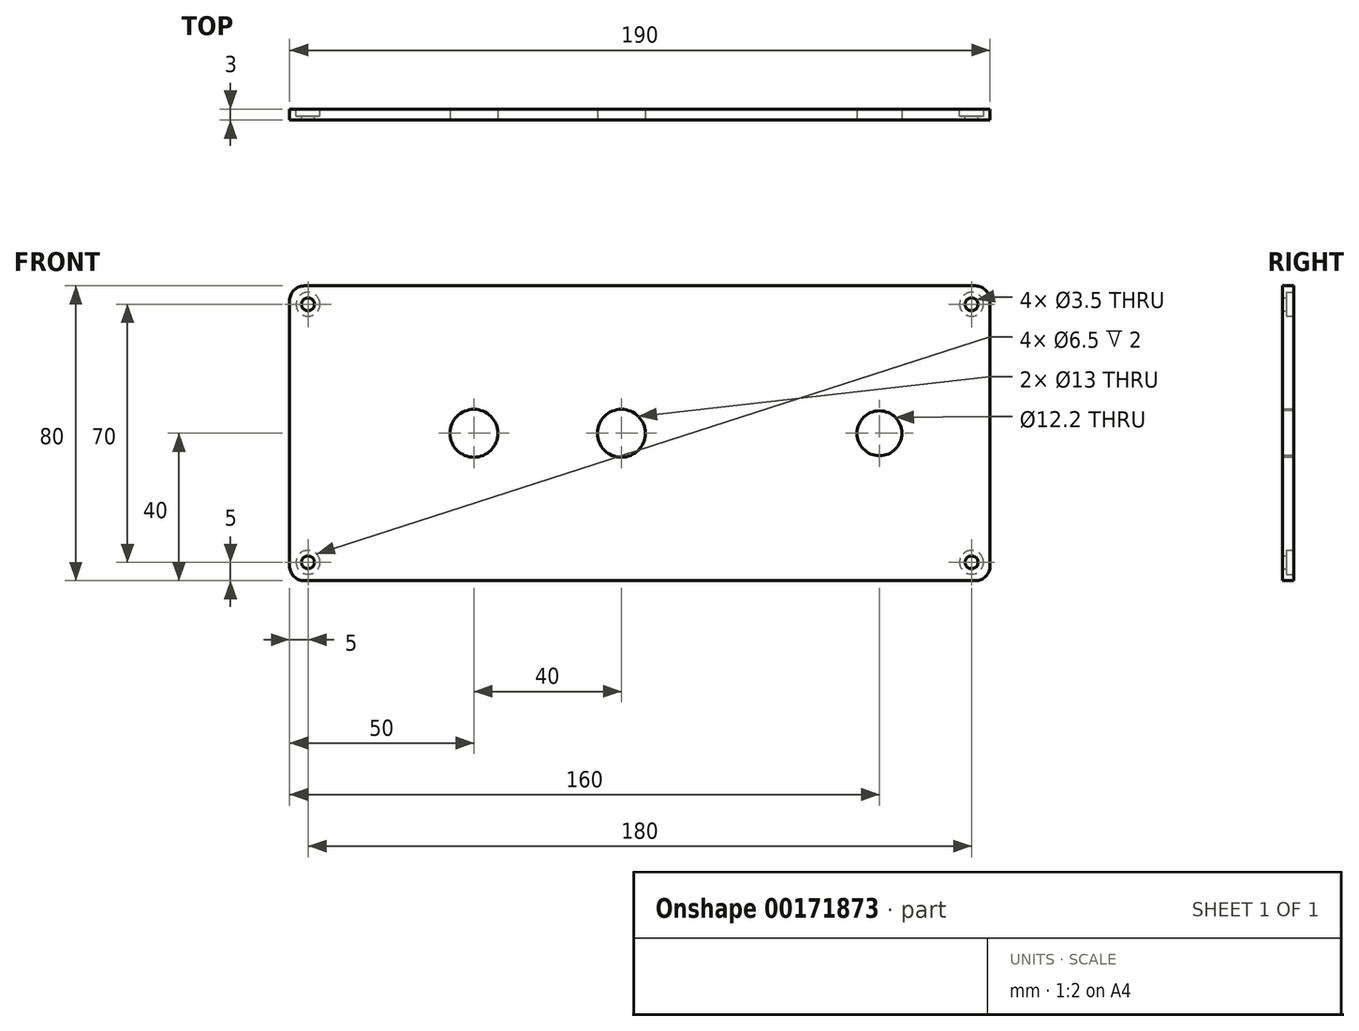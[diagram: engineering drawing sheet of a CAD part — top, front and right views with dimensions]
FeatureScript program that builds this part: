
annotation { "Feature Type Name" : "Feature", "Feature Type Description" : "" }
export const myFeature = defineFeature(function(context is Context, id is Id, definition is map)
    precondition{}
    {
        {
            var Q0;
            Q0=qCreatedBy(makeId("Front.planeOp"),FACE);
            var sketch = newSketch(context, id + "F0", { "sketchPlane" : qUnion([Q0])});
            skLineSegment(sketch, "E0.bottom", {"start": v(91, -40) * mm, "end": v(-91, -40) * mm});
            skLineSegment(sketch, "E0.top", {"start": v(91, 40) * mm, "end": v(-91, 40) * mm});
            skLineSegment(sketch, "E0.left", {"start": v(95, -36) * mm, "end": v(95, 36) * mm});
            skLineSegment(sketch, "E0.right", {"start": v(-95, -36) * mm, "end": v(-95, 36) * mm});
            skPoint(sketch, "E0.middle", {"position": v(0, 0) * mm});
            skLineSegment(sketch, "E1", {"start": v(-95.37, 0) * mm, "end": v(94.03, 0) * mm, "construction": true});
            skLineSegment(sketch, "E2", {"start": v(65, 41.22) * mm, "end": v(65, -44.39) * mm, "construction": true});
            skCircle(sketch, "E3", {"center": v(65, 0) * mm, "radius": 6.1 * mm});
            skPoint(sketch, "E4.visualSharp", {"position": v(-95, 40) * mm});
            skArc(sketch, "E4.filletArc", {"start": v(-91, 40) * mm, "mid": v(-93.83, 38.83) * mm, "end": v(-95, 36) * mm});
            skPoint(sketch, "E5.visualSharp", {"position": v(95, 40) * mm});
            skArc(sketch, "E5.filletArc", {"start": v(95, 36) * mm, "mid": v(93.83, 38.83) * mm, "end": v(91, 40) * mm});
            skPoint(sketch, "E6.visualSharp", {"position": v(95, -40) * mm});
            skArc(sketch, "E6.filletArc", {"start": v(91, -40) * mm, "mid": v(93.83, -38.83) * mm, "end": v(95, -36) * mm});
            skPoint(sketch, "E7.visualSharp", {"position": v(-95, -40) * mm});
            skArc(sketch, "E7.filletArc", {"start": v(-95, -36) * mm, "mid": v(-93.83, -38.83) * mm, "end": v(-91, -40) * mm});
            skPoint(sketch, "E8", {"position": v(65, -1.59) * mm});
            skLineSegment(sketch, "E9", {"start": v(0, 44.53) * mm, "end": v(0, -50.22) * mm, "construction": true});
            skLineSegment(sketch, "E10", {"start": v(-45, 47.95) * mm, "end": v(-45, -55.26) * mm, "construction": true});
            skCircle(sketch, "E11", {"center": v(-5, 0) * mm, "radius": 6.5 * mm});
            skCircle(sketch, "E12", {"center": v(-45, 0) * mm, "radius": 6.5 * mm});
            skLineSegment(sketch, "E13", {"start": v(-5, 53.53) * mm, "end": v(-5, -65.12) * mm, "construction": true});
            skSolve(sketch);
        }
        {
            var Q0;
            Q0=qSketchRegion(id+"F0",true);
            extrude(context, id + "F1", {"entities" : qUnion([Q0]), "oppositeDirection" : true, "depth" : 3 * mm});
        }
        {
            var Q0;
            Q0=makeQuery(id+"F1.opExtrude","CAP_FACE",FACE,{"disambiguationData":[OSD([sQuery(id+"F0.wireOp",EDGE,"E0.bottom"),sQuery(id+"F0.wireOp",EDGE,"E0.top"),sQuery(id+"F0.wireOp",EDGE,"E0.left"),sQuery(id+"F0.wireOp",EDGE,"E0.right"),sQuery(id+"F0.wireOp",EDGE,"4lk48Lhy-GrFW-aCKf-OnOU-HbCll7bjQ1xu"),sQuery(id+"F0.wireOp",EDGE,"0mMwZurY-QGWt-Txsz-sF5m-111nLayFImXw"),sQuery(id+"F0.wireOp",EDGE,"fLtfTxvr-Zha3-877r-iBnS-kihnbPZobVDH"),sQuery(id+"F0.wireOp",EDGE,"zJffz114-50WO-5Ndt-GAZO-3FlYt3vwu0AC"),sQuery(id+"F0.wireOp",EDGE,"zD25MLE3-AGDF-3XqF-6F3W-tQLZOGFrRJCD"),sQuery(id+"F0.wireOp",EDGE,"E3"),sQuery(id+"F0.wireOp",EDGE,"XLCIMhyg-kooL-GM2p-plMR-rza7P0k197HC"),sQuery(id+"F0.wireOp",EDGE,"3nWbJp3Q-z0hA-yKS7-ZoX7-3HNBMeytwRPm"),sQuery(id+"F0.wireOp",EDGE,"r6DEEYF7-k2yr-EeVm-i986-j8R7pWTw2rao"),sQuery(id+"F0.wireOp",EDGE,"dViKmaIw-3wPx-OBVm-rrEE-0ZRbR81GTxym"),sQuery(id+"F0.wireOp",EDGE,"E4.filletArc"),sQuery(id+"F0.wireOp",EDGE,"E5.filletArc"),sQuery(id+"F0.wireOp",EDGE,"E6.filletArc"),sQuery(id+"F0.wireOp",EDGE,"E7.filletArc")])],"isStart":false});
            var sketch = newSketch(context, id + "F2", { "sketchPlane" : qUnion([Q0])});
            skLineSegment(sketch, "E14", {"start": v(-103.47, 35) * mm, "end": v(120, 35) * mm, "construction": true});
            skLineSegment(sketch, "E15", {"start": v(-90, 42.73) * mm, "end": v(-90, -48.6) * mm, "construction": true});
            skLineSegment(sketch, "E16.MirrorCS", {"start": v(90, 42.73) * mm, "end": v(90, -48.6) * mm, "construction": true});
            skLineSegment(sketch, "E17.MirrorCS", {"start": v(-103.47, -35) * mm, "end": v(120, -35) * mm, "construction": true});
            skPoint(sketch, "E18", {"position": v(-90, 35) * mm});
            skPoint(sketch, "E19", {"position": v(90, 35) * mm});
            skPoint(sketch, "E20", {"position": v(90, -35) * mm});
            skPoint(sketch, "E21", {"position": v(-90, -35) * mm});
            skSolve(sketch);
        }
        {
            var Q0;
            Q0=sQuery(id+"F2.wireOp",VERTEX,"E18");
            var Q1;
            Q1=sQuery(id+"F2.wireOp",VERTEX,"E19");
            var Q2;
            Q2=sQuery(id+"F2.wireOp",VERTEX,"E20");
            var Q3;
            Q3=sQuery(id+"F2.wireOp",VERTEX,"E21");
            var Q4;
            Q4=makeQuery(id+"F1.opExtrude","SWEPT_BODY",BODY,{"disambiguationData":[OSD([sQuery(id+"F0.wireOp",EDGE,"E0.bottom"),sQuery(id+"F0.wireOp",EDGE,"E0.top"),sQuery(id+"F0.wireOp",EDGE,"E0.left"),sQuery(id+"F0.wireOp",EDGE,"E0.right"),sQuery(id+"F0.wireOp",EDGE,"4lk48Lhy-GrFW-aCKf-OnOU-HbCll7bjQ1xu"),sQuery(id+"F0.wireOp",EDGE,"0mMwZurY-QGWt-Txsz-sF5m-111nLayFImXw"),sQuery(id+"F0.wireOp",EDGE,"fLtfTxvr-Zha3-877r-iBnS-kihnbPZobVDH"),sQuery(id+"F0.wireOp",EDGE,"zJffz114-50WO-5Ndt-GAZO-3FlYt3vwu0AC"),sQuery(id+"F0.wireOp",EDGE,"zD25MLE3-AGDF-3XqF-6F3W-tQLZOGFrRJCD"),sQuery(id+"F0.wireOp",EDGE,"E3"),sQuery(id+"F0.wireOp",EDGE,"XLCIMhyg-kooL-GM2p-plMR-rza7P0k197HC"),sQuery(id+"F0.wireOp",EDGE,"3nWbJp3Q-z0hA-yKS7-ZoX7-3HNBMeytwRPm"),sQuery(id+"F0.wireOp",EDGE,"r6DEEYF7-k2yr-EeVm-i986-j8R7pWTw2rao"),sQuery(id+"F0.wireOp",EDGE,"dViKmaIw-3wPx-OBVm-rrEE-0ZRbR81GTxym"),sQuery(id+"F0.wireOp",EDGE,"E4.filletArc"),sQuery(id+"F0.wireOp",EDGE,"E5.filletArc"),sQuery(id+"F0.wireOp",EDGE,"E6.filletArc"),sQuery(id+"F0.wireOp",EDGE,"E7.filletArc")])]});
            hole(context, id + "F3", {"style" : HoleStyle.C_BORE, "endStyle" : HoleEndStyle.THROUGH, "holeDiameter" : 3.5 * mm, "cBoreDiameter" : 6.5 * mm, "cBoreDepth" : 2 * mm, "startFromSketch" : true, "locations" : qUnion([Q0, Q1, Q2, Q3]), "scope" : qUnion([Q4]), "isTappedThrough" : true});
        }
    });
